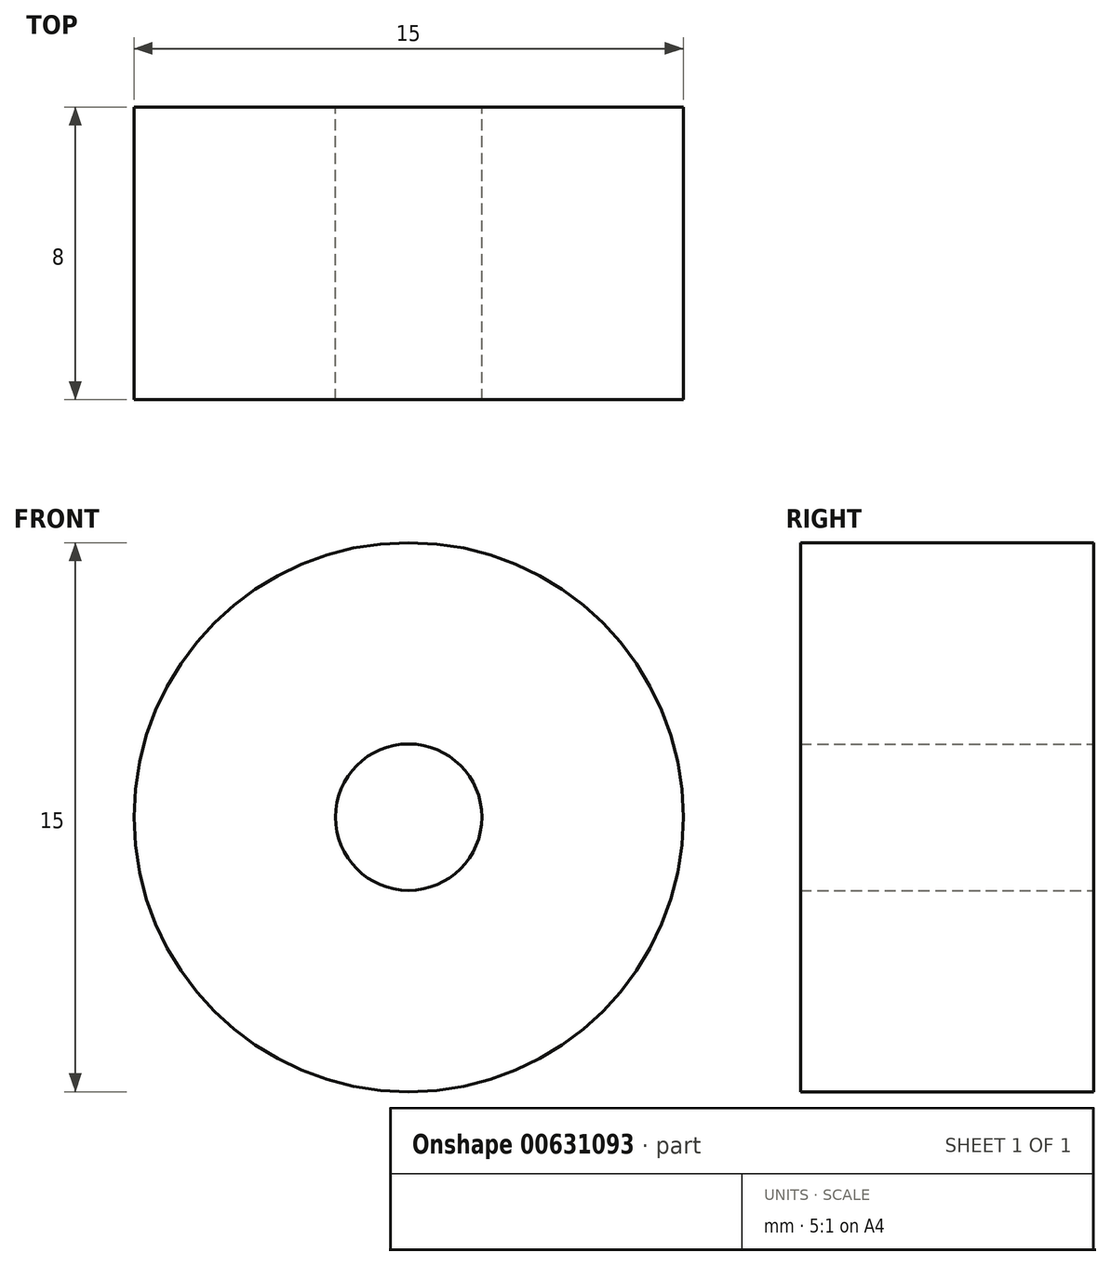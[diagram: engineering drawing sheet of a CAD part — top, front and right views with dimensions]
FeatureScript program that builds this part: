
annotation { "Feature Type Name" : "Feature", "Feature Type Description" : "" }
export const myFeature = defineFeature(function(context is Context, id is Id, definition is map)
    precondition{}
    {
        {
            var Q0;
            Q0=qCreatedBy(makeId("Front.planeOp"),FACE);
            var sketch = newSketch(context, id + "F0", { "sketchPlane" : qUnion([Q0])});
            skCircle(sketch, "E0", {"center": v(0, 0) * mm, "radius": 7.5 * mm});
            skSolve(sketch);
        }
        {
            var Q0;
            Q0=makeQuery(id+"F0.imprint","IMPRINT",FACE,{"disambiguationData":[TD([[makeQuery(id+"F0.imprint","IMPRINT",EDGE,{"derivedFrom":sQuery(id+"F0.wireOp",EDGE,"E0")}),1.0]])]});
            var sketch = newSketch(context, id + "F1", { "sketchPlane" : qUnion([Q0])});
            skCircle(sketch, "E1", {"center": v(0, 0) * mm, "radius": 2 * mm});
            skSolve(sketch);
        }
        {
            var Q0;
            Q0 = qSketchRegion(id + "F0", true);
            extrude(context, id + "F2", {"entities" : qUnion([Q0]), "depth" : 8 * mm, "offsetDistance" : 25 * mm});
        }
        {
            var Q0;
            Q0 = qSketchRegion(id + "F1", true);
            extrude(context, id + "F3", {"entities" : qUnion([Q0]), "operationType" : NewBodyOperationType.REMOVE, "endBound" : BoundingType.THROUGH_ALL, "depth" : 25 * mm, "offsetDistance" : 25 * mm});
        }
    });
